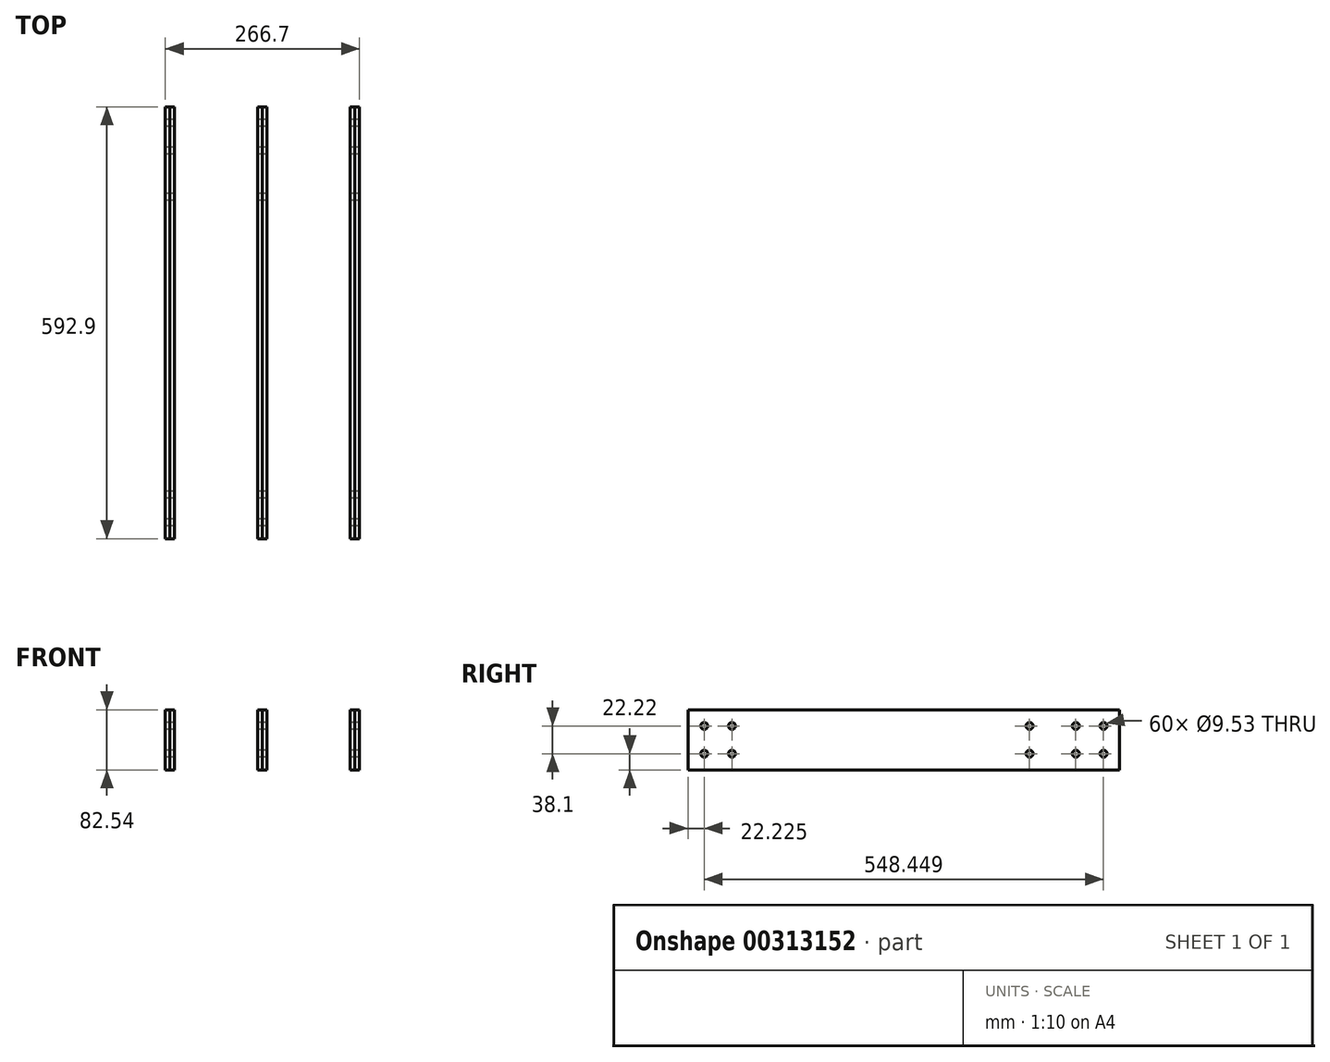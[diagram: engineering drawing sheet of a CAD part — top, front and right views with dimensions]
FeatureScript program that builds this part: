
annotation { "Feature Type Name" : "Feature", "Feature Type Description" : "" }
export const myFeature = defineFeature(function(context is Context, id is Id, definition is map)
    precondition{}
    {
        {
            var Q0;
            Q0=qCreatedBy(makeId("Top.planeOp"),FACE);
            var sketch = newSketch(context, id + "F0", { "sketchPlane" : qUnion([Q0])});
            skLineSegment(sketch, "E0.bottom", {"start": v(0, 0) * mm, "end": v(6.35, 0) * mm});
            skLineSegment(sketch, "E0.top", {"start": v(0, 592.9) * mm, "end": v(6.35, 592.9) * mm});
            skLineSegment(sketch, "E0.left", {"start": v(0, 0) * mm, "end": v(0, 592.9) * mm});
            skLineSegment(sketch, "E0.right", {"start": v(6.35, 0) * mm, "end": v(6.35, 592.9) * mm});
            skLineSegment(sketch, "E1.1.0.0", {"start": v(133.35, 0) * mm, "end": v(133.35, 592.9) * mm});
            skLineSegment(sketch, "E1.1.0.1", {"start": v(127, 0) * mm, "end": v(127, 592.9) * mm});
            skLineSegment(sketch, "E1.1.0.2", {"start": v(127, 592.9) * mm, "end": v(133.35, 592.9) * mm});
            skLineSegment(sketch, "E1.1.0.3", {"start": v(127, 0) * mm, "end": v(133.35, 0) * mm});
            skLineSegment(sketch, "E1.2.0.0", {"start": v(260.35, 0) * mm, "end": v(260.35, 592.9) * mm});
            skLineSegment(sketch, "E1.2.0.1", {"start": v(254, 0) * mm, "end": v(254, 592.9) * mm});
            skLineSegment(sketch, "E1.2.0.2", {"start": v(254, 592.9) * mm, "end": v(260.35, 592.9) * mm});
            skLineSegment(sketch, "E1.2.0.3", {"start": v(254, 0) * mm, "end": v(260.35, 0) * mm});
            skLineSegment(sketch, "E1.direction1", {"start": v(0, 0) * mm, "end": v(127, 0) * mm, "construction": true});
            skSolve(sketch);
        }
        {
            var Q0;
            Q0=qCreatedBy(makeId("Top.planeOp"),FACE);
            var sketch = newSketch(context, id + "F1", { "sketchPlane" : qUnion([Q0])});
            skLineSegment(sketch, "E2.bottom", {"start": v(6.35, 0) * mm, "end": v(12.7, 0) * mm});
            skLineSegment(sketch, "E2.top", {"start": v(6.35, 592.9) * mm, "end": v(12.7, 592.9) * mm});
            skLineSegment(sketch, "E2.left", {"start": v(6.35, 0) * mm, "end": v(6.35, 592.9) * mm});
            skLineSegment(sketch, "E2.right", {"start": v(12.7, 0) * mm, "end": v(12.7, 592.9) * mm});
            skLineSegment(sketch, "E3.1.0.0", {"start": v(139.7, 0) * mm, "end": v(139.7, 592.9) * mm});
            skLineSegment(sketch, "E3.1.0.1", {"start": v(133.35, 0) * mm, "end": v(133.35, 592.9) * mm});
            skLineSegment(sketch, "E3.1.0.2", {"start": v(133.35, 592.9) * mm, "end": v(139.7, 592.9) * mm});
            skLineSegment(sketch, "E3.1.0.3", {"start": v(133.35, 0) * mm, "end": v(139.7, 0) * mm});
            skLineSegment(sketch, "E3.2.0.0", {"start": v(266.7, 0) * mm, "end": v(266.7, 592.9) * mm});
            skLineSegment(sketch, "E3.2.0.1", {"start": v(260.35, 0) * mm, "end": v(260.35, 592.9) * mm});
            skLineSegment(sketch, "E3.2.0.2", {"start": v(260.35, 592.9) * mm, "end": v(266.7, 592.9) * mm});
            skLineSegment(sketch, "E3.2.0.3", {"start": v(260.35, 0) * mm, "end": v(266.7, 0) * mm});
            skLineSegment(sketch, "E3.direction1", {"start": v(6.35, 0) * mm, "end": v(133.35, 0) * mm, "construction": true});
            skSolve(sketch);
        }
        {
            var Q0;
            Q0=qSketchRegion(id+"F0",true);
            var Q1;
            Q1 = qSketchRegion(id + "F1", true);
            extrude(context, id + "F2", {"entities" : qUnion([Q0, Q1]), "endBound" : BoundingType.SYMMETRIC, "depth" : 82.55 * mm});
        }
        {
            var Q0;
            Q0=makeQuery(id+"F2.opExtrude","SWEPT_FACE",FACE,{"disambiguationData":[OSD([sQuery(id+"F0.wireOp",EDGE,"E0.left")])]});
            var sketch = newSketch(context, id + "F3", { "sketchPlane" : qUnion([Q0])});
            skCircle(sketch, "E4", {"center": v(-22.23, 19.05) * mm, "radius": 4.76 * mm});
            skCircle(sketch, "E5", {"center": v(-60.32, 19.05) * mm, "radius": 4.76 * mm});
            skCircle(sketch, "E6", {"center": v(-60.32, -19.05) * mm, "radius": 4.76 * mm});
            skCircle(sketch, "E7", {"center": v(-22.23, -19.05) * mm, "radius": 4.76 * mm});
            skCircle(sketch, "E8.1.0.0", {"center": v(-570.67, 19.05) * mm, "radius": 4.76 * mm});
            skCircle(sketch, "E8.1.0.1", {"center": v(-532.57, 19.05) * mm, "radius": 4.76 * mm});
            skCircle(sketch, "E8.1.0.2", {"center": v(-532.57, -19.05) * mm, "radius": 4.76 * mm});
            skCircle(sketch, "E8.1.0.3", {"center": v(-570.67, -19.05) * mm, "radius": 4.76 * mm});
            skCircle(sketch, "E9", {"center": v(-469.07, 19.05) * mm, "radius": 4.76 * mm});
            skCircle(sketch, "E10", {"center": v(-469.07, -19.05) * mm, "radius": 4.76 * mm});
            skSolve(sketch);
        }
        {
            var Q0;
            Q0 = qSketchRegion(id + "F3", true);
            extrude(context, id + "F4", {"entities" : qUnion([Q0]), "operationType" : NewBodyOperationType.REMOVE, "endBound" : BoundingType.THROUGH_ALL, "oppositeDirection" : true, "depth" : 25.4 * mm});
        }
    });
